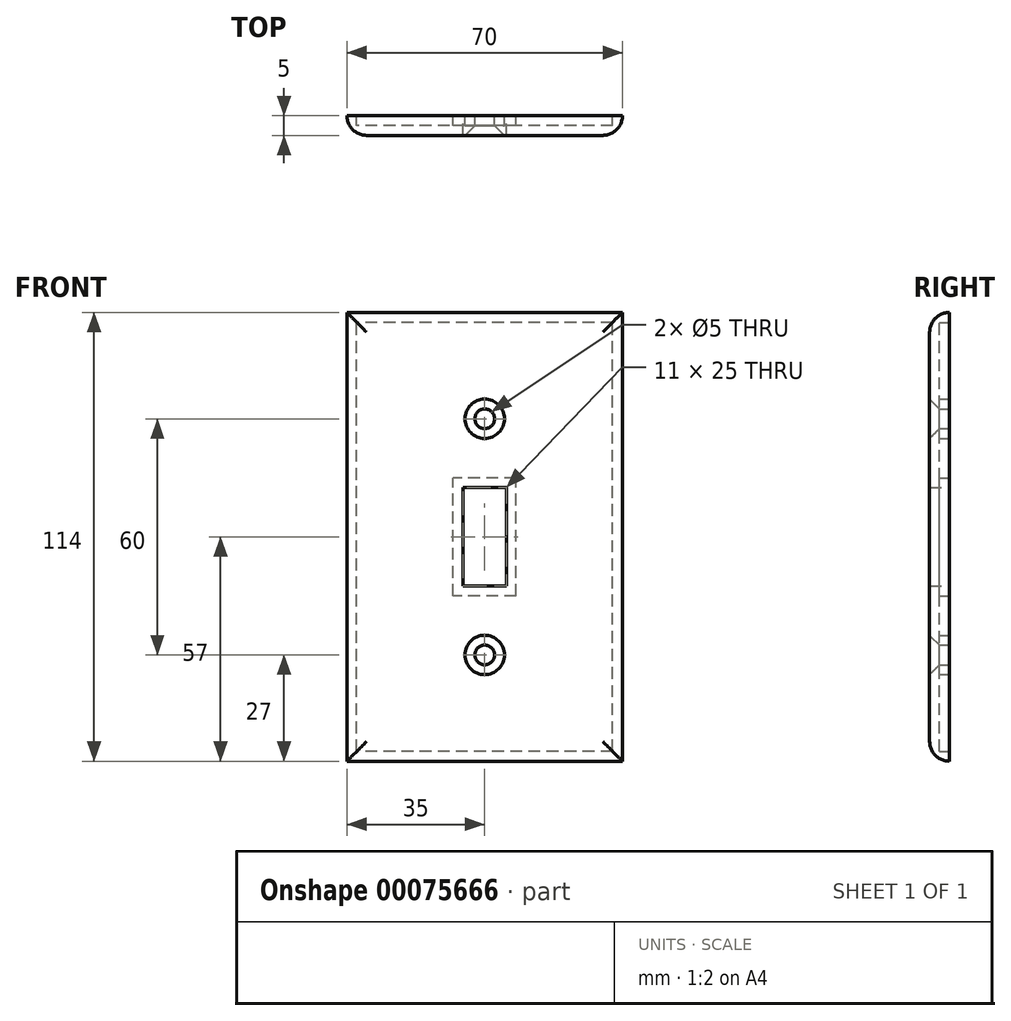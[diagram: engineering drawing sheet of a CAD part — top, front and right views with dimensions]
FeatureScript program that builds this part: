
annotation { "Feature Type Name" : "Feature", "Feature Type Description" : "" }
export const myFeature = defineFeature(function(context is Context, id is Id, definition is map)
    precondition{}
    {
        {
            var Q0;
            Q0=qCreatedBy(makeId("Front.planeOp"),FACE);
            var sketch = newSketch(context, id + "F0", { "sketchPlane" : qUnion([Q0])});
            skLineSegment(sketch, "E0.rect.bottom", {"start": v(35, -57) * mm, "end": v(-35, -57) * mm});
            skLineSegment(sketch, "E0.rect.top", {"start": v(35, 57) * mm, "end": v(-35, 57) * mm});
            skLineSegment(sketch, "E0.rect.left", {"start": v(35, -57) * mm, "end": v(35, 57) * mm});
            skLineSegment(sketch, "E0.rect.right", {"start": v(-35, -57) * mm, "end": v(-35, 57) * mm});
            skPoint(sketch, "E0.rect.middle", {"position": v(0, 0) * mm});
            skLineSegment(sketch, "E1.rect.bottom", {"start": v(5.5, -12.5) * mm, "end": v(-5.5, -12.5) * mm});
            skLineSegment(sketch, "E1.rect.top", {"start": v(5.5, 12.5) * mm, "end": v(-5.5, 12.5) * mm});
            skLineSegment(sketch, "E1.rect.left", {"start": v(5.5, -12.5) * mm, "end": v(5.5, 12.5) * mm});
            skLineSegment(sketch, "E1.rect.right", {"start": v(-5.5, -12.5) * mm, "end": v(-5.5, 12.5) * mm});
            skLineSegment(sketch, "E2", {"start": v(0, 30) * mm, "end": v(0, 12.5) * mm, "construction": true});
            skLineSegment(sketch, "E3", {"start": v(0, -12.5) * mm, "end": v(0, -30) * mm, "construction": true});
            skPoint(sketch, "E4", {"position": v(0, -30) * mm});
            skCircle(sketch, "E5", {"center": v(0, 30) * mm, "radius": 2.5 * mm});
            skCircle(sketch, "E6", {"center": v(0, -30) * mm, "radius": 2.5 * mm});
            skSolve(sketch);
        }
        {
            var Q0;
            Q0=makeQuery(id+"F0.imprint","IMPRINT",FACE,{"disambiguationData":[TD([[makeQuery(id+"F0.imprint","IMPRINT",EDGE,{"derivedFrom":sQuery(id+"F0.wireOp",EDGE,"E0.rect.bottom")}),-1.0]])]});
            extrude(context, id + "F1", {"entities" : qUnion([Q0]), "depth" : 5 * mm});
        }
        {
            var Q0;
            Q0=makeQuery(id+"F1.opExtrude","CAP_FACE",FACE,{"disambiguationData":[OSD([sQuery(id+"F0.wireOp",EDGE,"E0.rect.bottom"),sQuery(id+"F0.wireOp",EDGE,"E0.rect.top"),sQuery(id+"F0.wireOp",EDGE,"E0.rect.left"),sQuery(id+"F0.wireOp",EDGE,"E0.rect.right"),sQuery(id+"F0.wireOp",EDGE,"E1.rect.bottom"),sQuery(id+"F0.wireOp",EDGE,"E1.rect.top"),sQuery(id+"F0.wireOp",EDGE,"E1.rect.left"),sQuery(id+"F0.wireOp",EDGE,"E1.rect.right"),sQuery(id+"F0.wireOp",EDGE,"dd9179df-2efc-4905-b1f9-0efd251ffeb2"),sQuery(id+"F0.wireOp",EDGE,"d5df8e78-6afb-4b83-a791-8970aa5ca6f3")])],"isStart":true});
            shell(context, id + "F2", {"entities" : qUnion([Q0]), "thickness" : 2.5 * mm});
        }
        {
            var Q0;
            Q0=makeQuery(id+"F1.opExtrude","CAP_FACE",FACE,{"disambiguationData":[OSD([sQuery(id+"F0.wireOp",EDGE,"E0.rect.bottom"),sQuery(id+"F0.wireOp",EDGE,"E0.rect.top"),sQuery(id+"F0.wireOp",EDGE,"E0.rect.left"),sQuery(id+"F0.wireOp",EDGE,"E0.rect.right"),sQuery(id+"F0.wireOp",EDGE,"E1.rect.bottom"),sQuery(id+"F0.wireOp",EDGE,"E1.rect.top"),sQuery(id+"F0.wireOp",EDGE,"E1.rect.left"),sQuery(id+"F0.wireOp",EDGE,"E1.rect.right")])],"isStart":false});
            var sketch = newSketch(context, id + "F3", { "sketchPlane" : qUnion([Q0])});
            skLineSegment(sketch, "E7.0", {"start": v(0, 30) * mm, "end": v(0, 12.5) * mm, "construction": true});
            skLineSegment(sketch, "E8.0", {"start": v(0, -12.5) * mm, "end": v(0, -30) * mm, "construction": true});
            skPoint(sketch, "E9", {"position": v(0, 30) * mm});
            skPoint(sketch, "E10", {"position": v(0, -30) * mm});
            skSolve(sketch);
        }
        {
            var Q0;
            Q0=sQuery(id+"F3.wireOp",VERTEX,"E9");
            var Q1;
            Q1=sQuery(id+"F3.wireOp",VERTEX,"E10");
            var Q2;
            Q2=makeQuery(id+"F1.opExtrude","SWEPT_BODY",BODY,{"disambiguationData":[OSD([sQuery(id+"F0.wireOp",EDGE,"E0.rect.bottom"),sQuery(id+"F0.wireOp",EDGE,"E0.rect.top"),sQuery(id+"F0.wireOp",EDGE,"E0.rect.left"),sQuery(id+"F0.wireOp",EDGE,"E0.rect.right"),sQuery(id+"F0.wireOp",EDGE,"E1.rect.bottom"),sQuery(id+"F0.wireOp",EDGE,"E1.rect.top"),sQuery(id+"F0.wireOp",EDGE,"E1.rect.left"),sQuery(id+"F0.wireOp",EDGE,"E1.rect.right"),sQuery(id+"F0.wireOp",EDGE,"E5"),sQuery(id+"F0.wireOp",EDGE,"E6")])]});
            hole(context, id + "F4", {"style" : HoleStyle.C_SINK, "holeDiameter" : 5 * mm, "cSinkDiameter" : 10 * mm, "endStyle" : HoleEndStyle.THROUGH, "locations" : qUnion([Q0, Q1]), "scope" : qUnion([Q2]), "cSinkAngle" : 90 * degree});
        }
        {
            var Q0;
            Q0=makeQuery(id+"F1.opExtrude","CAP_EDGE",EDGE,{"disambiguationData":[OSD([sQuery(id+"F0.wireOp",EDGE,"E0.rect.right")])],"isStart":false});
            var Q1;
            Q1=makeQuery(id+"F1.opExtrude","CAP_EDGE",EDGE,{"disambiguationData":[OSD([sQuery(id+"F0.wireOp",EDGE,"E0.rect.top")])],"isStart":false});
            var Q2;
            Q2=makeQuery(id+"F1.opExtrude","CAP_EDGE",EDGE,{"disambiguationData":[OSD([sQuery(id+"F0.wireOp",EDGE,"E0.rect.left")])],"isStart":false});
            var Q3;
            Q3=makeQuery(id+"F1.opExtrude","CAP_EDGE",EDGE,{"disambiguationData":[OSD([sQuery(id+"F0.wireOp",EDGE,"E0.rect.bottom")])],"isStart":false});
            fillet(context, id + "F5", {"entities" : qUnion([Q0, Q1, Q2, Q3]), "radius" : 5 * mm, "tangentPropagation" : true, "allowEdgeOverflow" : false});
        }
    });
